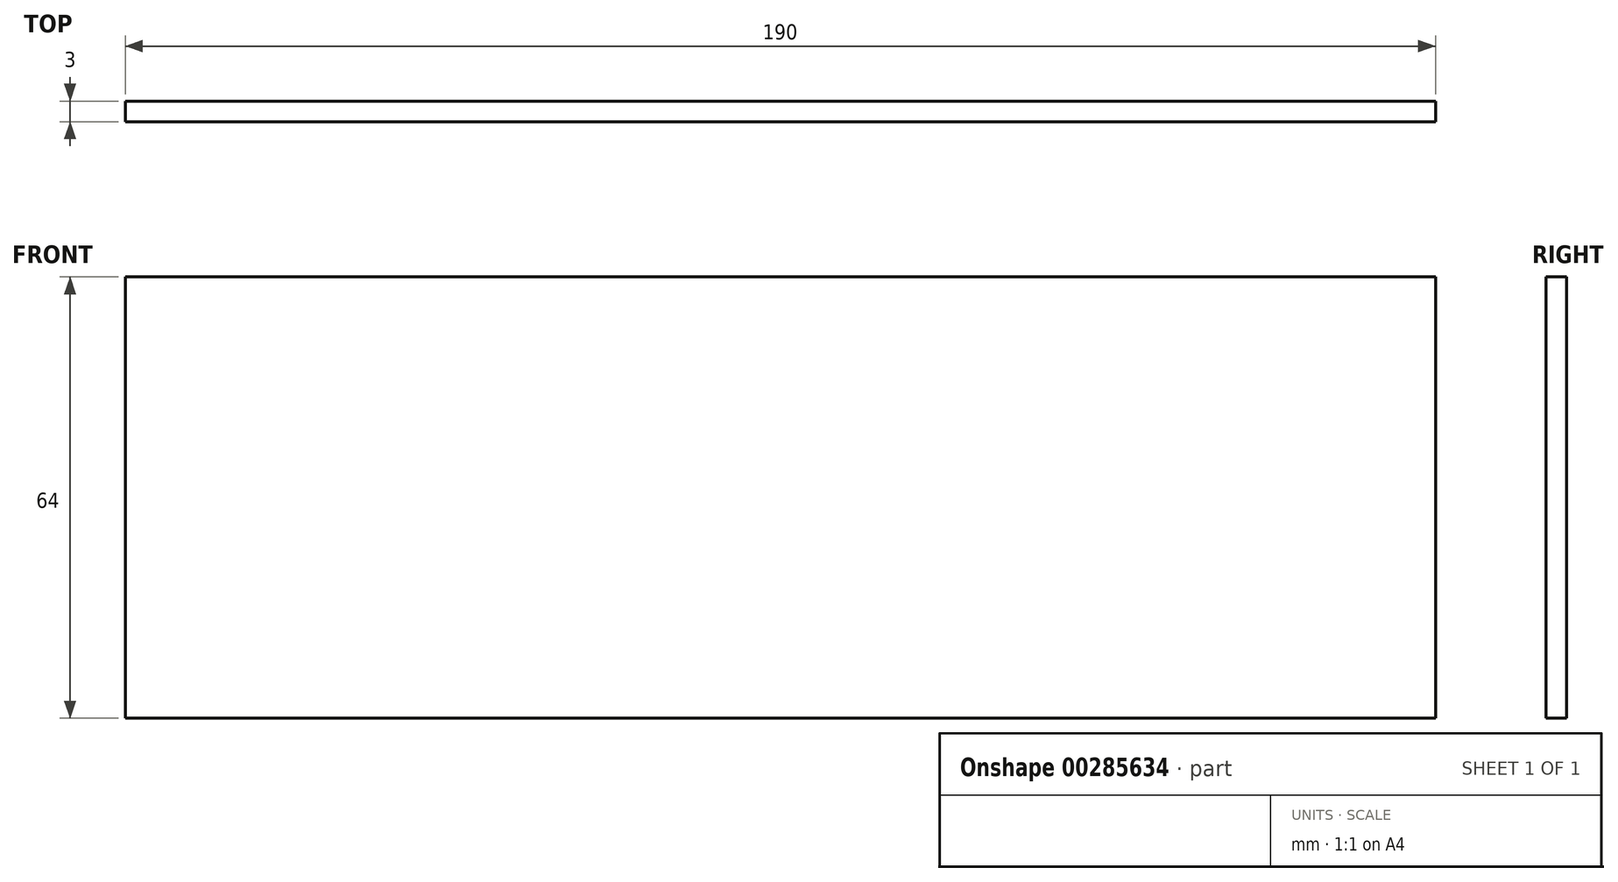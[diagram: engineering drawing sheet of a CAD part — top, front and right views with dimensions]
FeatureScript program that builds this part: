
annotation { "Feature Type Name" : "Feature", "Feature Type Description" : "" }
export const myFeature = defineFeature(function(context is Context, id is Id, definition is map)
    precondition{}
    {
        {
            var Q0;
            Q0=qCreatedBy(makeId("Front.planeOp"),FACE);
            var sketch = newSketch(context, id + "F0", { "sketchPlane" : qUnion([Q0])});
            skLineSegment(sketch, "E0.bottom", {"start": v(-95, 32) * mm, "end": v(95, 32) * mm});
            skLineSegment(sketch, "E0.top", {"start": v(-95, -32) * mm, "end": v(95, -32) * mm});
            skLineSegment(sketch, "E0.left", {"start": v(-95, 32) * mm, "end": v(-95, -32) * mm});
            skLineSegment(sketch, "E0.right", {"start": v(95, 32) * mm, "end": v(95, -32) * mm});
            skPoint(sketch, "E0.middle", {"position": v(0, 0) * mm});
            skSolve(sketch);
        }
        {
            var Q0;
            Q0=makeQuery(id+"F0.imprint","IMPRINT",FACE,{"disambiguationData":[TD([[makeQuery(id+"F0.imprint","IMPRINT",EDGE,{"derivedFrom":sQuery(id+"F0.wireOp",EDGE,"E0.bottom")}),-1.0]])]});
            extrude(context, id + "F1", {"entities" : qUnion([Q0]), "depth" : 3 * mm});
        }
    });
